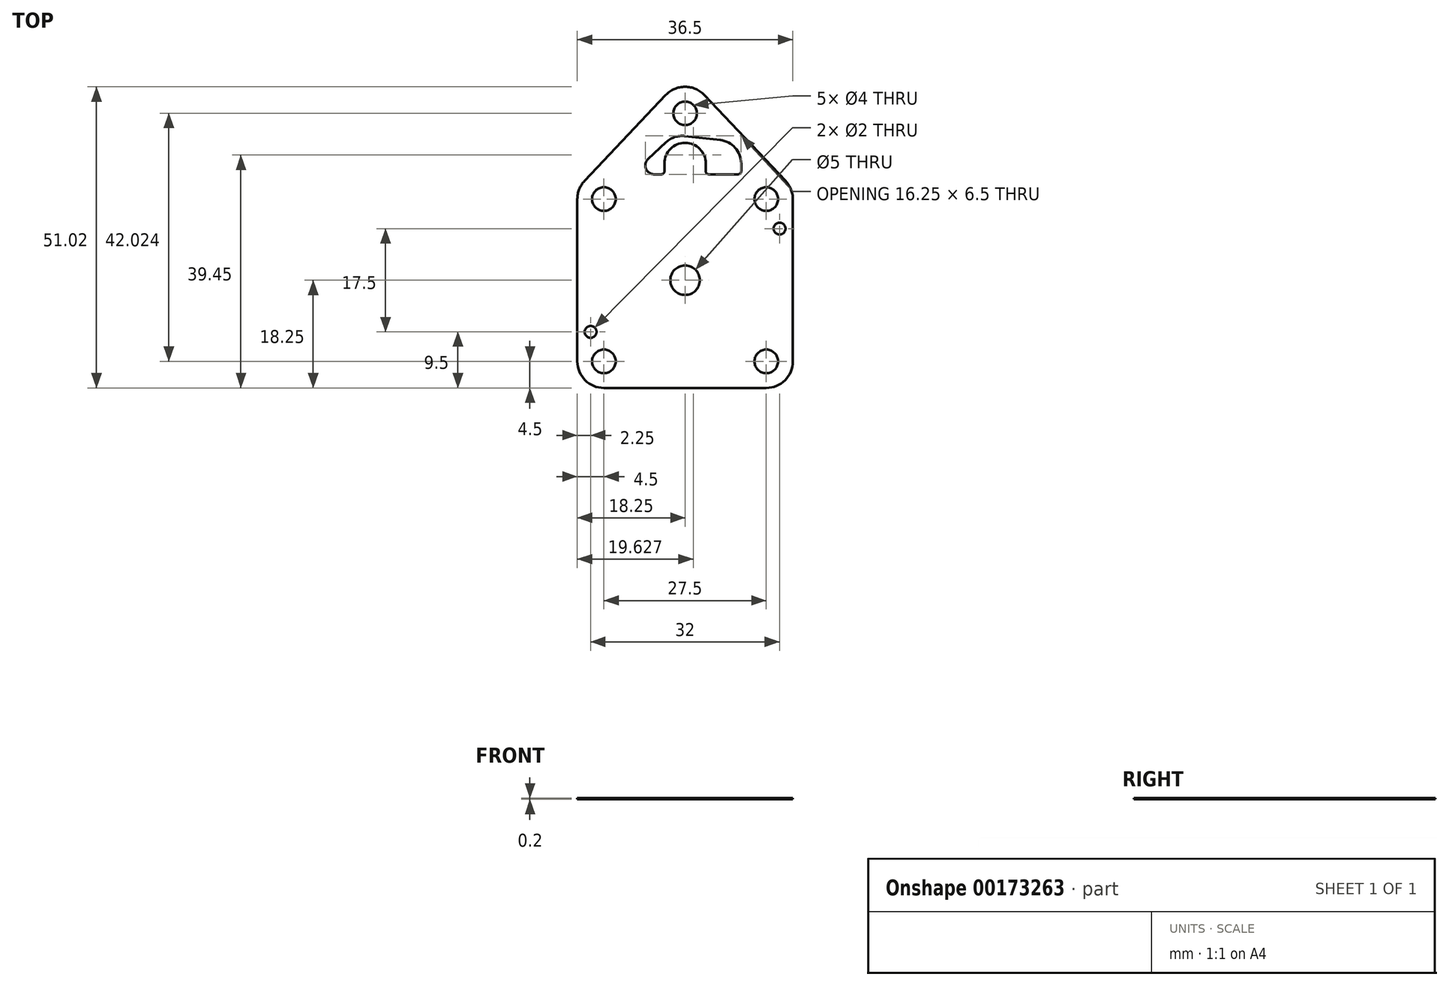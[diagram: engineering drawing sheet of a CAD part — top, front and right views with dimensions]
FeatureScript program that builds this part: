
annotation { "Feature Type Name" : "Feature", "Feature Type Description" : "" }
export const myFeature = defineFeature(function(context is Context, id is Id, definition is map)
    precondition{}
    {
        {
            var Q0;
            Q0=qCreatedBy(makeId("Top.planeOp"),FACE);
            var sketch = newSketch(context, id + "F0", { "sketchPlane" : qUnion([Q0])});
            skCircle(sketch, "E0", {"center": v(0, 0) * mm, "radius": 2.5 * mm});
            skLineSegment(sketch, "E1.bottom", {"start": v(13.75, 13.75) * mm, "end": v(-13.75, 13.75) * mm, "construction": true});
            skLineSegment(sketch, "E1.top", {"start": v(13.75, -13.75) * mm, "end": v(-13.75, -13.75) * mm, "construction": true});
            skLineSegment(sketch, "E1.left", {"start": v(13.75, 13.75) * mm, "end": v(13.75, -13.75) * mm, "construction": true});
            skLineSegment(sketch, "E1.right", {"start": v(-13.75, 13.75) * mm, "end": v(-13.75, -13.75) * mm, "construction": true});
            skCircle(sketch, "E2", {"center": v(-13.75, 13.75) * mm, "radius": 2 * mm});
            skCircle(sketch, "E3", {"center": v(-13.75, -13.75) * mm, "radius": 2 * mm});
            skLineSegment(sketch, "E4", {"start": v(0, 34.75) * mm, "end": v(0, -21.42) * mm, "construction": true});
            skCircle(sketch, "E5.MirrorC", {"center": v(13.75, 13.75) * mm, "radius": 2 * mm});
            skCircle(sketch, "E6.MirrorC", {"center": v(13.75, -13.75) * mm, "radius": 2 * mm});
            skCircle(sketch, "E7", {"center": v(0, 28.27) * mm, "radius": 2 * mm});
            skLineSegment(sketch, "E8", {"start": v(-3.27, 31.37) * mm, "end": v(-17.02, 16.84) * mm});
            skLineSegment(sketch, "E9", {"start": v(-18.25, 13.75) * mm, "end": v(-18.25, -13.75) * mm});
            skLineSegment(sketch, "E10", {"start": v(-13.75, -18.25) * mm, "end": v(13.75, -18.25) * mm});
            skLineSegment(sketch, "E11.MirrorCS", {"start": v(18.25, 13.75) * mm, "end": v(18.25, -13.75) * mm});
            skLineSegment(sketch, "E12.MirrorCS", {"start": v(3.27, 31.37) * mm, "end": v(17.02, 16.84) * mm});
            skArc(sketch, "E13", {"start": v(-3.27, 31.37) * mm, "mid": v(0, 23.77) * mm, "end": v(3.27, 31.37) * mm, "construction": true});
            skArc(sketch, "E14", {"start": v(3.27, 31.37) * mm, "mid": v(0, 32.77) * mm, "end": v(-3.27, 31.37) * mm});
            skArc(sketch, "E15", {"start": v(-18.25, 13.75) * mm, "mid": v(-9.57, 12.08) * mm, "end": v(-17.02, 16.84) * mm, "construction": true});
            skArc(sketch, "E16", {"start": v(-17.02, 16.84) * mm, "mid": v(-17.93, 15.42) * mm, "end": v(-18.25, 13.75) * mm});
            skArc(sketch, "E17", {"start": v(-18.25, -13.75) * mm, "mid": v(-16.93, -16.93) * mm, "end": v(-13.75, -18.25) * mm});
            skArc(sketch, "E18", {"start": v(-13.75, -18.25) * mm, "mid": v(-10.57, -10.57) * mm, "end": v(-18.25, -13.75) * mm, "construction": true});
            skArc(sketch, "E19.MirrorCS", {"start": v(17.02, 16.84) * mm, "mid": v(17.93, 15.42) * mm, "end": v(18.25, 13.75) * mm});
            skArc(sketch, "E20.MirrorCS", {"start": v(18.25, -13.75) * mm, "mid": v(16.93, -16.93) * mm, "end": v(13.75, -18.25) * mm});
            skSolve(sketch);
        }
        {
            var Q0;
            Q0=makeQuery(id+"F0.imprint","IMPRINT",FACE,{"disambiguationData":[TD([[makeQuery(id+"F0.imprint","IMPRINT",EDGE,{"derivedFrom":sQuery(id+"F0.wireOp",EDGE,"E0")}),-1.0]])]});
            extrude(context, id + "F1", {"entities" : qUnion([Q0]), "depth" : .2 * mm});
        }
        {
            var Q0;
            Q0=makeQuery(id+"F1.opExtrude","CAP_FACE",FACE,{"disambiguationData":[OSD([sQuery(id+"F0.wireOp",EDGE,"E0"),sQuery(id+"F0.wireOp",EDGE,"E2"),sQuery(id+"F0.wireOp",EDGE,"E3"),sQuery(id+"F0.wireOp",EDGE,"E5.MirrorC"),sQuery(id+"F0.wireOp",EDGE,"E6.MirrorC"),sQuery(id+"F0.wireOp",EDGE,"E7"),sQuery(id+"F0.wireOp",EDGE,"E8"),sQuery(id+"F0.wireOp",EDGE,"E9"),sQuery(id+"F0.wireOp",EDGE,"E10"),sQuery(id+"F0.wireOp",EDGE,"E11.MirrorCS"),sQuery(id+"F0.wireOp",EDGE,"E12.MirrorCS"),sQuery(id+"F0.wireOp",EDGE,"E14"),sQuery(id+"F0.wireOp",EDGE,"E16"),sQuery(id+"F0.wireOp",EDGE,"E17"),sQuery(id+"F0.wireOp",EDGE,"E19.MirrorCS"),sQuery(id+"F0.wireOp",EDGE,"E20.MirrorCS")])],"isStart":false});
            var sketch = newSketch(context, id + "F2", { "sketchPlane" : qUnion([Q0])});
            skLineSegment(sketch, "E21", {"start": v(0, 0) * mm, "end": v(0, 28.27) * mm, "construction": true});
            skArc(sketch, "E22", {"start": v(3.5, 19.77) * mm, "mid": v(0, 23.27) * mm, "end": v(-3.5, 19.77) * mm});
            skPoint(sketch, "E23", {"position": v(-13.75, 13.75) * mm});
            skLineSegment(sketch, "E24", {"start": v(-5.25, 17.95) * mm, "end": v(-4, 17.95) * mm});
            skArc(sketch, "E25", {"start": v(-6.27, 20.55) * mm, "mid": v(-6.65, 18.9) * mm, "end": v(-5.25, 17.95) * mm});
            skLineSegment(sketch, "E26", {"start": v(-3.5, 19.77) * mm, "end": v(3.5, 19.77) * mm, "construction": true});
            skLineSegment(sketch, "E27", {"start": v(-3.5, 19.77) * mm, "end": v(-3.5, 18.45) * mm});
            skArc(sketch, "E28", {"start": v(-4, 17.95) * mm, "mid": v(-3.65, 18.1) * mm, "end": v(-3.5, 18.45) * mm});
            skLineSegment(sketch, "E29.MirrorCS", {"start": v(3.5, 19.77) * mm, "end": v(3.5, 18.45) * mm});
            skArc(sketch, "E30.MirrorCS", {"start": v(4, 17.95) * mm, "mid": v(3.65, 18.1) * mm, "end": v(3.5, 18.45) * mm});
            skLineSegment(sketch, "E31.trimOffspring", {"start": v(4, 17.95) * mm, "end": v(9, 17.95) * mm});
            skArc(sketch, "E32", {"start": v(9, 17.95) * mm, "mid": v(9.35, 18.1) * mm, "end": v(9.5, 18.45) * mm});
            skLineSegment(sketch, "E33", {"start": v(-6.27, 20.55) * mm, "end": v(-3.22, 23.38) * mm});
            skLineSegment(sketch, "E34", {"start": v(9.5, 18.45) * mm, "end": v(9.5, 19.77) * mm});
            skLineSegment(sketch, "E35", {"start": v(-0.05, 24.42) * mm, "end": v(5.95, 23.75) * mm});
            skArc(sketch, "E36", {"start": v(9.5, 19.77) * mm, "mid": v(8.48, 22.44) * mm, "end": v(5.95, 23.75) * mm});
            skArc(sketch, "E37", {"start": v(-0.05, 24.42) * mm, "mid": v(-1.75, 24.25) * mm, "end": v(-3.22, 23.38) * mm});
            skCircle(sketch, "E38", {"center": v(16, 8.75) * mm, "radius": 1 * mm});
            skCircle(sketch, "E39", {"center": v(-16, -8.75) * mm, "radius": 1 * mm});
            skPoint(sketch, "E40", {"position": v(13.75, 13.75) * mm});
            skPoint(sketch, "E41", {"position": v(-13.75, -13.75) * mm});
            skSolve(sketch);
        }
        {
            var Q0;
            Q0=makeQuery(id+"F2.imprint","IMPRINT",FACE,{"disambiguationData":[TD([[makeQuery(id+"F2.imprint","IMPRINT",EDGE,{"derivedFrom":sQuery(id+"F2.wireOp",EDGE,"E22")}),-1.0]])]});
            var Q1;
            Q1=makeQuery(id+"F2.imprint","IMPRINT",FACE,{"disambiguationData":[TD([[makeQuery(id+"F2.imprint","IMPRINT",EDGE,{"derivedFrom":sQuery(id+"F2.wireOp",EDGE,"E39")}),1.0]])]});
            var Q2;
            Q2=makeQuery(id+"F2.imprint","IMPRINT",FACE,{"disambiguationData":[TD([[makeQuery(id+"F2.imprint","IMPRINT",EDGE,{"derivedFrom":sQuery(id+"F2.wireOp",EDGE,"E38")}),1.0]])]});
            extrude(context, id + "F3", {"entities" : qUnion([Q0, Q1, Q2]), "operationType" : NewBodyOperationType.REMOVE, "endBound" : BoundingType.THROUGH_ALL, "oppositeDirection" : true, "depth" : 25 * mm});
        }
    });
